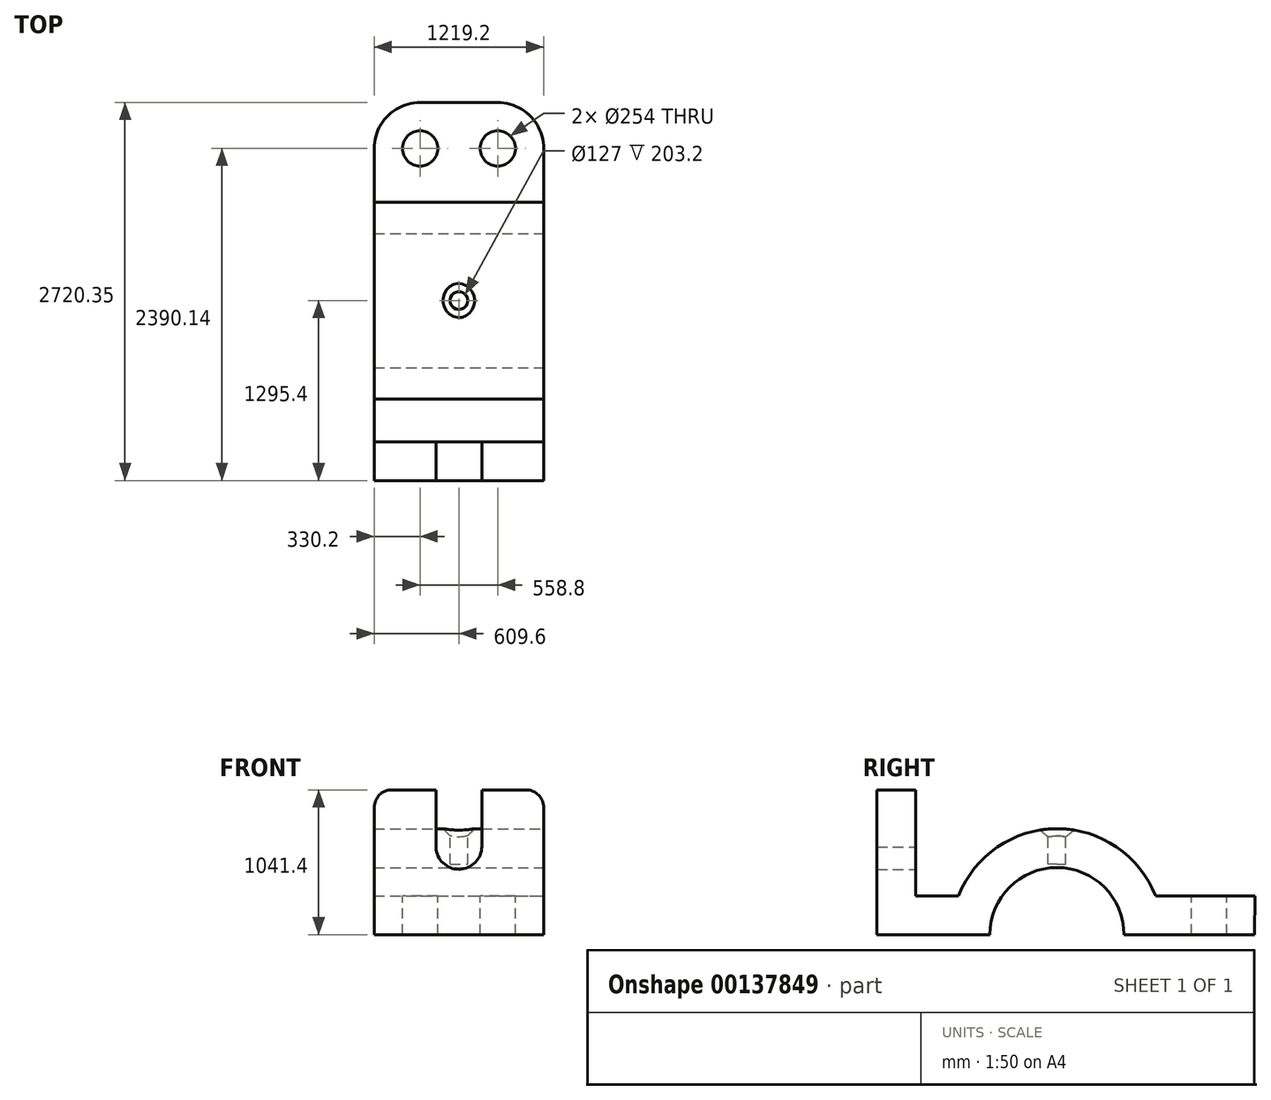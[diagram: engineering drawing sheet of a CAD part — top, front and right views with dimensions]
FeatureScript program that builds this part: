
annotation { "Feature Type Name" : "Feature", "Feature Type Description" : "" }
export const myFeature = defineFeature(function(context is Context, id is Id, definition is map)
    precondition{}
    {
        {
            var Q0;
            Q0=qCreatedBy(makeId("Front.planeOp"),FACE);
            var sketch = newSketch(context, id + "F0", { "sketchPlane" : qUnion([Q0])});
            skLineSegment(sketch, "E0", {"start": v(0, 0) * mm, "end": v(609.6, 0) * mm});
            skLineSegment(sketch, "E1", {"start": v(609.6, 0) * mm, "end": v(609.6, 914.4) * mm});
            skLineSegment(sketch, "E2", {"start": v(0, 0) * mm, "end": v(-609.6, 0) * mm});
            skLineSegment(sketch, "E3", {"start": v(-609.6, 0) * mm, "end": v(-609.6, 914.4) * mm});
            skLineSegment(sketch, "E4", {"start": v(-482.6, 1041.4) * mm, "end": v(-165.01, 1041.4) * mm});
            skLineSegment(sketch, "E5", {"start": v(482.6, 1041.4) * mm, "end": v(165.1, 1041.4) * mm});
            skArc(sketch, "E6", {"start": v(165.1, 635) * mm, "mid": v(2.7, 469.92) * mm, "end": v(-165.01, 629.58) * mm});
            skLineSegment(sketch, "E7", {"start": v(-165.01, 629.58) * mm, "end": v(-165.01, 1041.4) * mm});
            skLineSegment(sketch, "E8", {"start": v(165.1, 635) * mm, "end": v(165.1, 1041.4) * mm});
            skPoint(sketch, "E9.visualSharp", {"position": v(-609.6, 1041.4) * mm});
            skArc(sketch, "E9.filletArc", {"start": v(-482.6, 1041.4) * mm, "mid": v(-572.4, 1004.2) * mm, "end": v(-609.6, 914.4) * mm});
            skPoint(sketch, "E10.visualSharp", {"position": v(609.6, 1041.4) * mm});
            skArc(sketch, "E10.filletArc", {"start": v(609.6, 914.4) * mm, "mid": v(572.4, 1004.2) * mm, "end": v(482.6, 1041.4) * mm});
            skSolve(sketch);
        }
        {
            var Q0;
            Q0 = qSketchRegion(id + "F0", true);
            extrude(context, id + "F1", {"entities" : qUnion([Q0]), "depth" : 279.4 * mm});
        }
        {
            var Q0;
            Q0=qCreatedBy(makeId("Right.planeOp"),FACE);
            var sketch = newSketch(context, id + "F2", { "sketchPlane" : qUnion([Q0])});
            skLineSegment(sketch, "E11", {"start": v(0, 0) * mm, "end": v(533.4, 0) * mm});
            skArc(sketch, "E12", {"start": v(1498.6, 0) * mm, "mid": v(1016, 482.6) * mm, "end": v(533.4, 0) * mm});
            skLineSegment(sketch, "E13", {"start": v(2212.18, 0) * mm, "end": v(2438.4, 0) * mm});
            skLineSegment(sketch, "E14", {"start": v(1498.6, 0) * mm, "end": v(2212.18, 0) * mm});
            skLineSegment(sketch, "E15", {"start": v(0, 279.4) * mm, "end": v(307.07, 279.4) * mm});
            skArc(sketch, "E16", {"start": v(307.07, 279.4) * mm, "mid": v(1016, 762) * mm, "end": v(1724.93, 279.4) * mm});
            skLineSegment(sketch, "E17", {"start": v(1724.93, 279.4) * mm, "end": v(2440.95, 279.4) * mm});
            skLineSegment(sketch, "E18", {"start": v(2440.95, 279.4) * mm, "end": v(2438.4, 0) * mm});
            skLineSegment(sketch, "E19", {"start": v(0, 279.4) * mm, "end": v(0, 0) * mm});
            skSolve(sketch);
        }
        {
            var Q0;
            Q0 = qSketchRegion(id + "F2", true);
            extrude(context, id + "F3", {"entities" : qUnion([Q0]), "operationType" : NewBodyOperationType.ADD, "endBound" : BoundingType.SYMMETRIC, "oppositeDirection" : true, "depth" : 1219.2 * mm});
        }
        {
            var Q0;
            Q0=makeQuery(id+"F3.opExtrude","CAP_EDGE",EDGE,{"disambiguationData":[OSD([sQuery(id+"F2.wireOp",EDGE,"E18")])],"isStart":false});
            fillet(context, id + "F4", {"entities" : qUnion([Q0]), "radius" : 330.2 * mm, "tangentPropagation" : true, "allowEdgeOverflow" : false});
        }
        {
            var Q0;
            Q0=makeQuery(id+"F3.opExtrude","CAP_EDGE",EDGE,{"disambiguationData":[OSD([sQuery(id+"F2.wireOp",EDGE,"E18")])],"isStart":true});
            fillet(context, id + "F5", {"entities" : qUnion([Q0]), "radius" : 330.2 * mm, "tangentPropagation" : true, "allowEdgeOverflow" : false});
        }
        {
            var Q0;
            Q0=makeQuery(id+"F3.opExtrude","SWEPT_FACE",FACE,{"disambiguationData":[OSD([sQuery(id+"F2.wireOp",EDGE,"E17")])]});
            var sketch = newSketch(context, id + "F6", { "sketchPlane" : qUnion([Q0])});
            skCircle(sketch, "E20", {"center": v(279.4, 2110.74) * mm, "radius": 127 * mm});
            skCircle(sketch, "E21", {"center": v(-279.4, 2110.74) * mm, "radius": 127 * mm});
            skSolve(sketch);
        }
        {
            var Q0;
            Q0 = qSketchRegion(id + "F6", true);
            extrude(context, id + "F7", {"entities" : qUnion([Q0]), "operationType" : NewBodyOperationType.REMOVE, "endBound" : BoundingType.THROUGH_ALL, "oppositeDirection" : true, "depth" : 25.4 * mm});
        }
        {
            var Q0;
            Q0=makeQuery(id+"F3.opExtrude","SWEPT_FACE",FACE,{"disambiguationData":[OSD([sQuery(id+"F2.wireOp",EDGE,"E13"),sQuery(id+"F2.wireOp",EDGE,"E14")])]});
            cPlane(context, id + "F8", {"entities" : qUnion([Q0]), "cplaneType" : CPlaneType.OFFSET, "offset" : 762 * mm, "oppositeDirection" : true, "width" : 152.4 * mm, "height" : 152.4 * mm});
        }
        {
            var Q0;
            Q0=qCreatedBy(id+"F8.planeOp",FACE);
            var sketch = newSketch(context, id + "F9", { "sketchPlane" : qUnion([Q0])});
            skCircle(sketch, "E22", {"center": v(0, -1016) * mm, "radius": 63.5 * mm});
            skCircle(sketch, "E23", {"center": v(0, -1016) * mm, "radius": 127 * mm});
            skSolve(sketch);
        }
        {
            var Q0;
            Q0=makeQuery(id+"F9.imprint","IMPRINT",FACE,{"disambiguationData":[TD([[makeQuery(id+"F9.imprint","IMPRINT",EDGE,{"derivedFrom":sQuery(id+"F9.wireOp",EDGE,"E22")}),1.0]])]});
            extrude(context, id + "F10", {"entities" : qUnion([Q0]), "operationType" : NewBodyOperationType.REMOVE, "depth" : 254 * mm});
        }
        {
            var Q0;
            Q0=makeQuery(id+"F10.boolean.opBoolean","INTERSECT",EDGE,{"derivedFrom":[makeQuery(id+"F3.opExtrude","SWEPT_FACE",FACE,{"disambiguationData":[OSD([sQuery(id+"F2.wireOp",EDGE,"E16")])]}),makeQuery(id+"F10.opExtrude","SWEPT_FACE",FACE,{"disambiguationData":[OSD([sQuery(id+"F9.wireOp",EDGE,"E22")])]})]});
            chamfer(context, id + "F11", {"entities" : qUnion([Q0]), "width" : 50.8 * mm, "tangentPropagation" : true});
        }
    });
